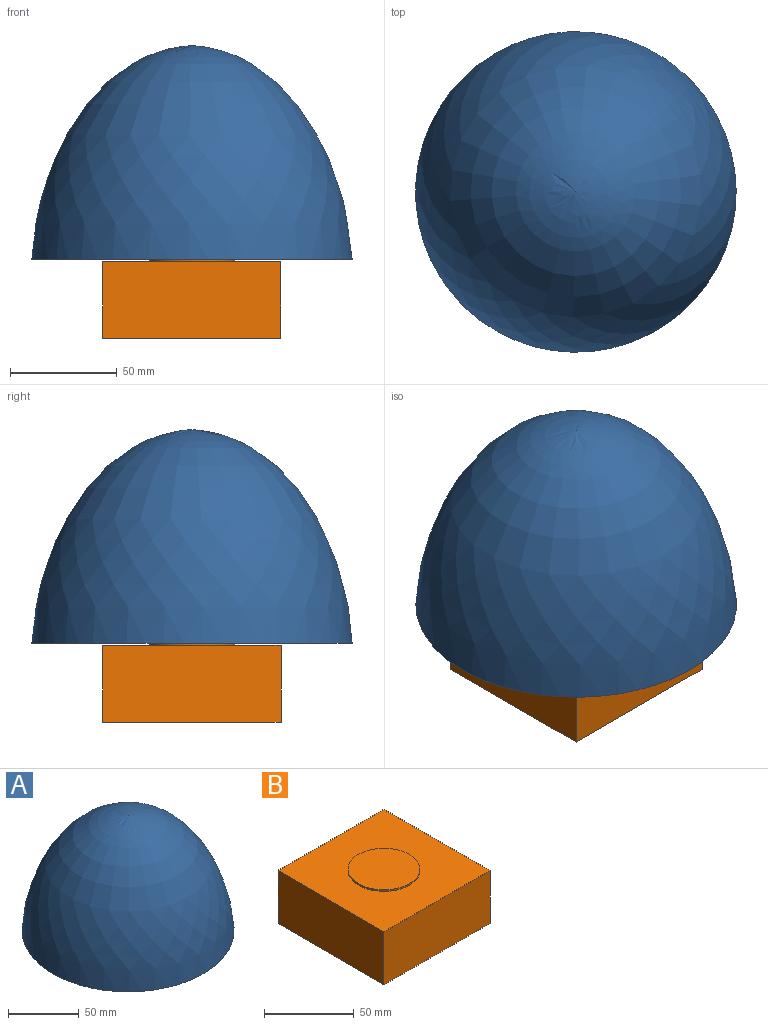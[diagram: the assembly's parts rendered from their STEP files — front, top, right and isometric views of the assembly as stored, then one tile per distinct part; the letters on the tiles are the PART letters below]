
ASSEMBLY  parts=2 mates=2
PART A: 3 faces, bbox 150x150x100 mm
  f0: revolved ~150x150mm, area 42031.9mm2, adj f2
  f1: plane 20x20mm, normal (0,0,-1), area 314.2mm2, adj f2
  f2: revolved ~150x150mm, area 22519.8mm2, adj f0,f1
PART B: 8 faces, bbox 83.3x83.3x37 mm
  f0: plane 83.33x36mm, normal (1,0,0), area 3000mm2, adj f1,f3,f4,f5
  f1: plane 83.33x36mm, normal (0,1,0), area 3000mm2, adj f0,f2,f4,f5
  f2: plane 83.33x36mm, normal (-1,0,0), area 3000mm2, adj f1,f3,f4,f5
  f3: plane 83.33x36mm, normal (0,-1,0), area 3000mm2, adj f0,f2,f4,f5
  f4: plane 83.33x83.33mm, normal (0,0,1), area 5687.8mm2, adj f0,f1,f2,f3,f6
  f5: plane 83.33x83.33mm, normal (0,0,-1), area 6944.4mm2, adj f0,f1,f2,f3
  f6: cylinder r=20mm len=40mm, axis (0,0,-1), area 125.7mm2, adj f4,f7
  f7: plane 40x40mm, normal (0,0,1), area 1256.6mm2, adj f6
PLACE A rot(axis=(0,0,1),43deg) t=(-11.24,-14.79,37.04)mm
PLACE B t=(-11.24,-14.79,0.04)mm fixed
MATE cylindrical A.f1 <-> B.f6  axis (0,0,-1) through (-11.24,-14.79,37.04)mm
MATE planar A.f1 <-> B.f6  axis (0,0,1) through (-11.24,-14.79,37.04)mm
